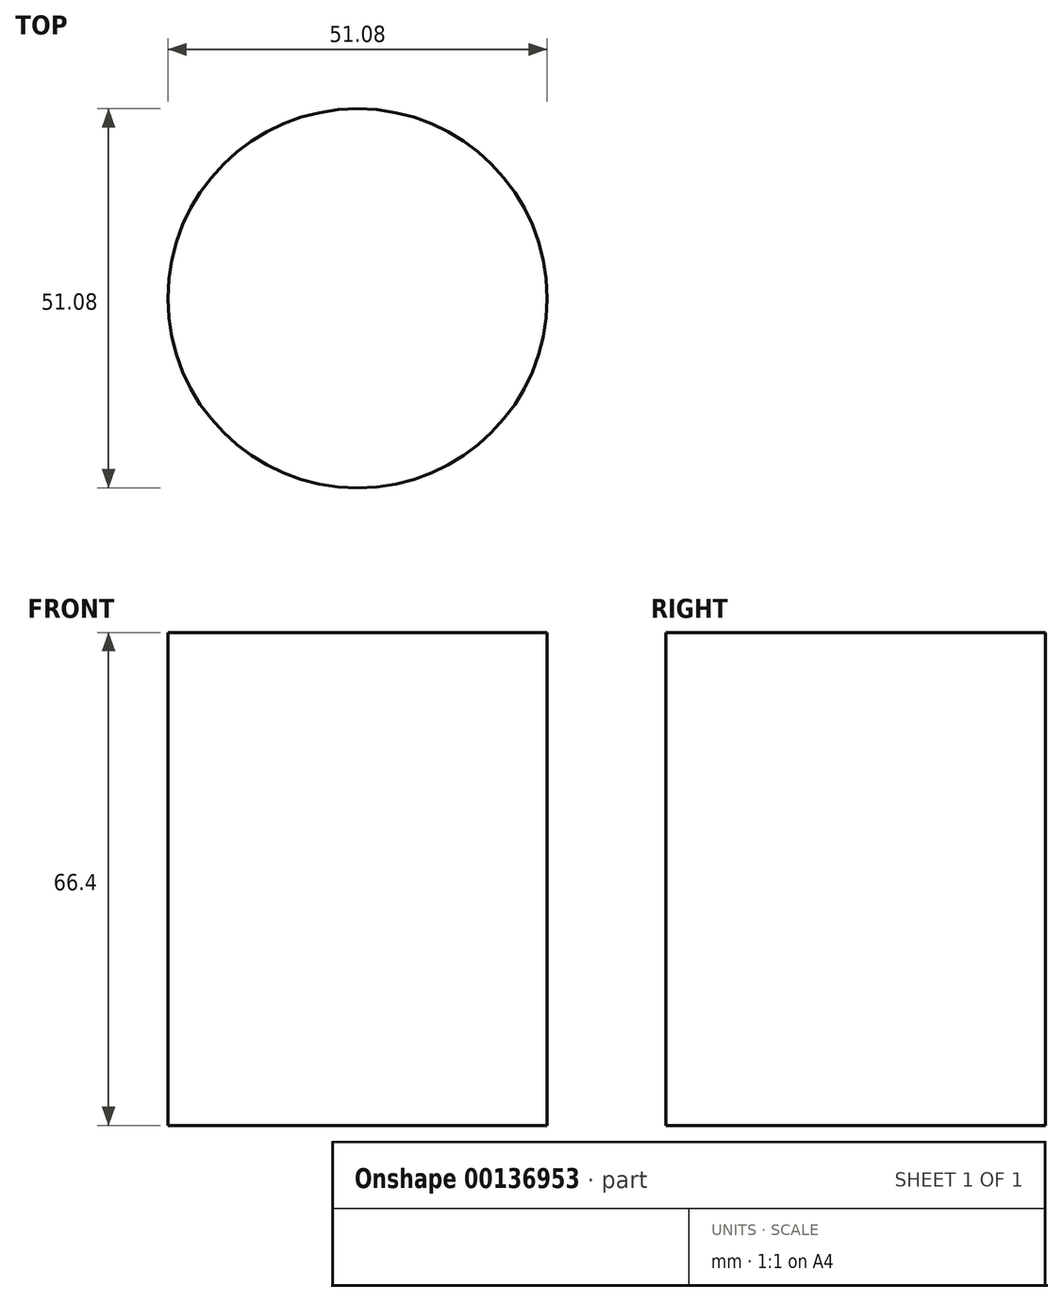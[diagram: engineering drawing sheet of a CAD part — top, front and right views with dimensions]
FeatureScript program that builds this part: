
annotation { "Feature Type Name" : "Feature", "Feature Type Description" : "" }
export const myFeature = defineFeature(function(context is Context, id is Id, definition is map)
    precondition{}
    {
        {
            var Q0;
            Q0=qCreatedBy(makeId("Top.planeOp"),FACE);
            var sketch = newSketch(context, id + "F0", { "sketchPlane" : qUnion([Q0])});
            skCircle(sketch, "E0", {"center": v(0, 0) * mm, "radius": 25.54 * mm});
            skSolve(sketch);
        }
        {
            var Q0;
            Q0=makeQuery(id+"F0.imprint","IMPRINT",FACE,{"disambiguationData":[TD([[makeQuery(id+"F0.imprint","IMPRINT",EDGE,{"derivedFrom":sQuery(id+"F0.wireOp",EDGE,"E0")}),1.0]])]});
            extrude(context, id + "F1", {"entities" : qUnion([Q0]), "depth" : 66.4 * mm, "offsetDistance" : 25 * mm});
        }
    });
